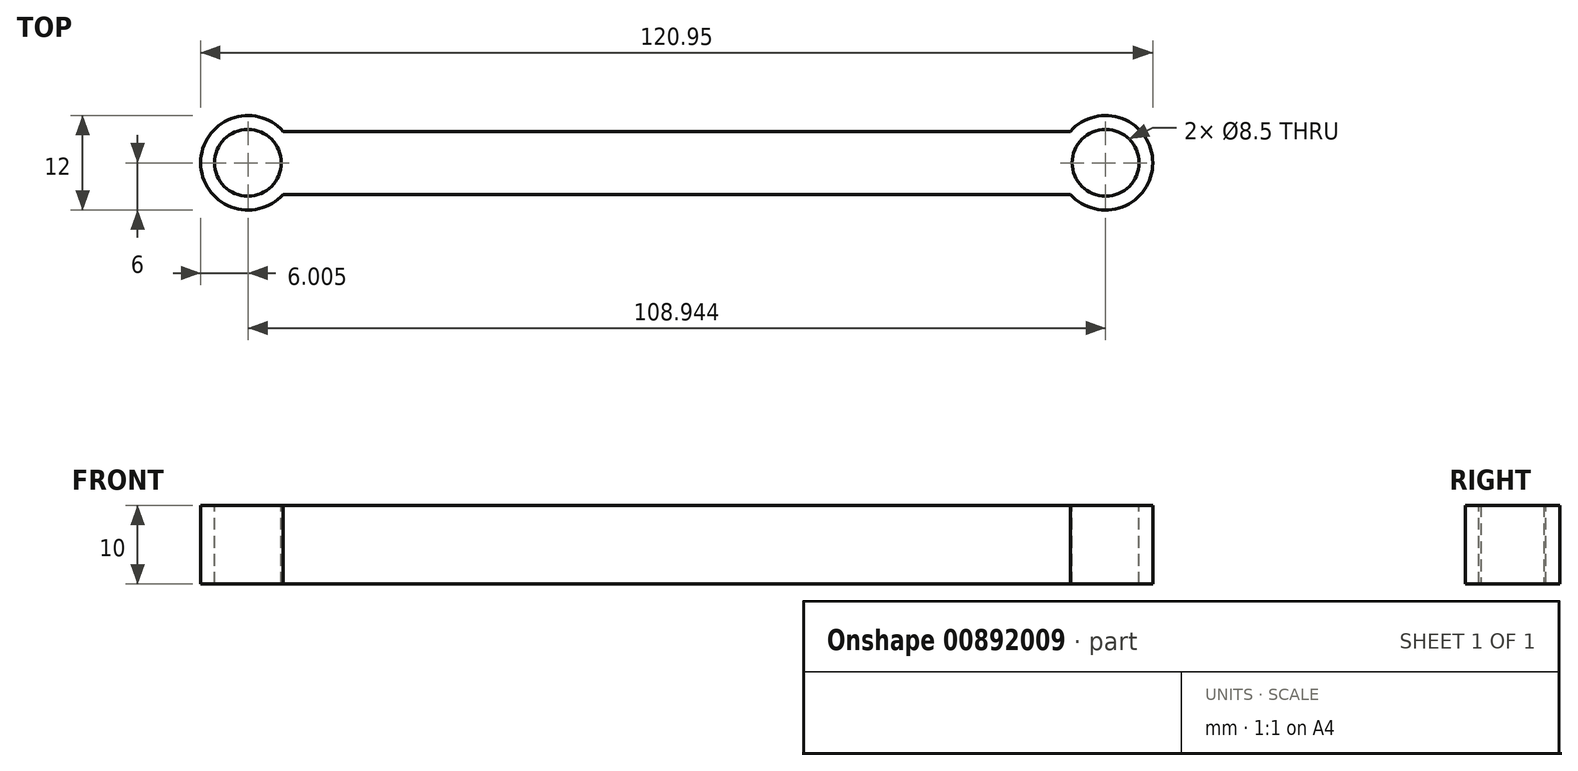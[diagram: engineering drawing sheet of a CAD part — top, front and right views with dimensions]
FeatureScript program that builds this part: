
annotation { "Feature Type Name" : "Feature", "Feature Type Description" : "" }
export const myFeature = defineFeature(function(context is Context, id is Id, definition is map)
    precondition{}
    {
        {
            var Q0;
            Q0=qCreatedBy(makeId("Top.planeOp"),FACE);
            var sketch = newSketch(context, id + "F0", { "sketchPlane" : qUnion([Q0])});
            skCircle(sketch, "E0", {"center": v(-33.98, 0) * mm, "radius": 6 * mm});
            skSolve(sketch);
        }
        {
            var Q0;
            Q0 = qSketchRegion(id + "F0", true);
            extrude(context, id + "F1", {"entities" : qUnion([Q0]), "depth" : 10 * mm, "offsetDistance" : 25 * mm});
        }
        {
            var Q0;
            Q0=makeQuery(id+"F1.opExtrude","CAP_FACE",FACE,{"disambiguationData":[OSD([sQuery(id+"F0.wireOp",EDGE,"E0")])],"isStart":false});
            var sketch = newSketch(context, id + "F2", { "sketchPlane" : qUnion([Q0])});
            skCircle(sketch, "E1", {"center": v(-33.98, 0) * mm, "radius": 4.25 * mm});
            skSolve(sketch);
        }
        {
            var Q0;
            Q0=makeQuery(id+"F2.imprint","IMPRINT",FACE,{"disambiguationData":[TD([[makeQuery(id+"F2.imprint","IMPRINT",EDGE,{"derivedFrom":sQuery(id+"F2.wireOp",EDGE,"E1")}),1.0]])]});
            extrude(context, id + "F3", {"entities" : qUnion([Q0]), "operationType" : NewBodyOperationType.REMOVE, "oppositeDirection" : true, "depth" : 10 * mm, "offsetDistance" : 25 * mm});
        }
        {
            var Q0;
            Q0=makeQuery(id+"F1.opExtrude","CAP_FACE",FACE,{"disambiguationData":[OSD([sQuery(id+"F0.wireOp",EDGE,"E0")])],"isStart":true});
            var sketch = newSketch(context, id + "F4", { "sketchPlane" : qUnion([Q0])});
            skLineSegment(sketch, "E2.bottom", {"start": v(-29.5, 4) * mm, "end": v(20.5, 4) * mm});
            skLineSegment(sketch, "E2.top", {"start": v(-29.5, -4) * mm, "end": v(20.5, -4) * mm});
            skLineSegment(sketch, "E2.left", {"start": v(-29.5, 4) * mm, "end": v(-29.5, -4) * mm});
            skLineSegment(sketch, "E2.right", {"start": v(20.5, 4) * mm, "end": v(20.5, -4) * mm});
            skSolve(sketch);
        }
        {
            var Q0;
            Q0 = qSketchRegion(id + "F4", true);
            extrude(context, id + "F5", {"entities" : qUnion([Q0]), "operationType" : NewBodyOperationType.ADD, "depth" : -10 * mm, "offsetDistance" : 25 * mm});
        }
        {
            var Q0;
            Q0=makeQuery(id+"F1.opExtrude","SWEPT_BODY",BODY,{"disambiguationData":[OSD([sQuery(id+"F0.wireOp",EDGE,"E0")])]});
            var Q1;
            Q1=makeQuery(id+"F5.opExtrude","SWEPT_FACE",FACE,{"disambiguationData":[OSD([sQuery(id+"F4.wireOp",EDGE,"E2.right")])]});
            mirror(context, id + "F6", {"operationType" : NewBodyOperationType.ADD, "entities" : qUnion([Q0]), "mirrorPlane" : qUnion([Q1])});
        }
    });
